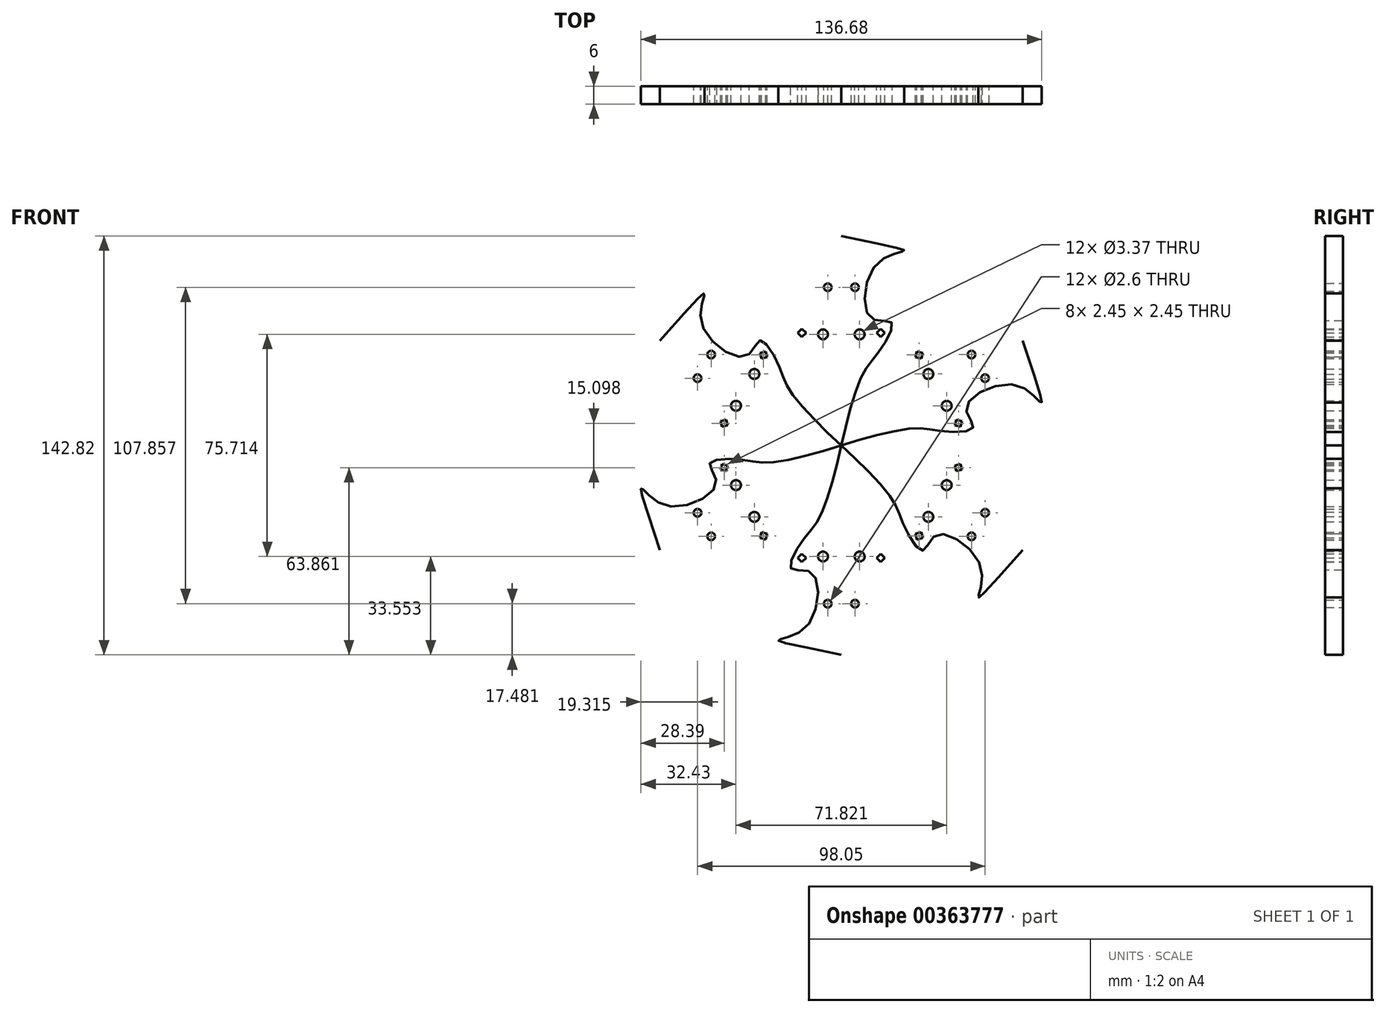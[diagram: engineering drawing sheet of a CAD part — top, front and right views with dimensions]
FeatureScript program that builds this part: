
annotation { "Feature Type Name" : "Feature", "Feature Type Description" : "" }
export const myFeature = defineFeature(function(context is Context, id is Id, definition is map)
    precondition{}
    {
        {
            var Q0;
            Q0=qCreatedBy(makeId("Front.planeOp"),FACE);
            var sketch = newSketch(context, id + "F0", { "sketchPlane" : qUnion([Q0])});
            skLineSegment(sketch, "E0", {"start": v(0, 0) * mm, "end": v(0, 66.43) * mm, "construction": true});
            skFitSpline(sketch, "E1", {"points": [v(0, 71.4) * mm, v(20.6, 65.97) * mm, v(11.17, 60.88) * mm, v(10.13, 43.35) * mm, v(17.12, 41.96) * mm, v(12.86, 32) * mm, v(7.45, 24.61) * mm, v(0, 0) * mm], "startDerivative": vector(349.85, -73.2) * mm, "endDerivative": vector(-30.6, -141.84) * mm});
            skCircle(sketch, "E2", {"center": v(6.25, 37.86) * mm, "radius": 1.68 * mm});
            skCircle(sketch, "E3", {"center": v(4.64, 53.93) * mm, "radius": 1.3 * mm});
            skLineSegment(sketch, "E4.bottom", {"start": v(-13.44, 39.79) * mm, "end": v(-12.02, 38.37) * mm});
            skLineSegment(sketch, "E4.top", {"start": v(-14.85, 38.37) * mm, "end": v(-13.44, 36.96) * mm});
            skLineSegment(sketch, "E4.left", {"start": v(-13.44, 39.79) * mm, "end": v(-14.85, 38.37) * mm});
            skLineSegment(sketch, "E4.right", {"start": v(-12.02, 38.37) * mm, "end": v(-13.44, 36.96) * mm});
            skLineSegment(sketch, "E5.MirrorCS", {"start": v(12.02, 38.37) * mm, "end": v(13.44, 36.96) * mm});
            skLineSegment(sketch, "E6.MirrorCS", {"start": v(13.44, 39.79) * mm, "end": v(14.85, 38.37) * mm});
            skLineSegment(sketch, "E7.MirrorCS", {"start": v(14.85, 38.37) * mm, "end": v(13.44, 36.96) * mm});
            skLineSegment(sketch, "E8.MirrorCS", {"start": v(13.44, 39.79) * mm, "end": v(12.02, 38.37) * mm});
            skCircle(sketch, "E9.MirrorC", {"center": v(-4.64, 53.93) * mm, "radius": 1.3 * mm});
            skCircle(sketch, "E10.MirrorC", {"center": v(-6.25, 37.86) * mm, "radius": 1.68 * mm});
            skFitSpline(sketch, "E11.MirrorCS", {"points": [v(0, 71.4) * mm, v(-20.6, 65.97) * mm, v(-11.17, 60.88) * mm, v(-10.13, 43.35) * mm, v(-17.12, 41.96) * mm, v(-12.86, 32) * mm, v(-7.45, 24.61) * mm, v(0, 0) * mm], "startDerivative": vector(-349.85, -73.2) * mm, "endDerivative": vector(30.6, -141.84) * mm});
            skSolve(sketch);
        }
        {
            var Q0;
            Q0 = qSketchRegion(id + "F0", true);
            extrude(context, id + "F1", {"entities" : qUnion([Q0]), "depth" : 6 * mm});
        }
        {
            var Q0;
            Q0=qCreatedBy(makeId("Right.planeOp"),FACE);
            var sketch = newSketch(context, id + "F2", { "sketchPlane" : qUnion([Q0])});
            skLineSegment(sketch, "E12", {"start": v(0, 0) * mm, "end": v(-63.75, 0) * mm, "construction": true});
            skSolve(sketch);
        }
        {
            var Q0;
            Q0=makeQuery(id+"F1.opExtrude","SWEPT_BODY",BODY,{"disambiguationData":[OSD([sQuery(id+"F0.wireOp",EDGE,"E1"),sQuery(id+"F0.wireOp",EDGE,"E2"),sQuery(id+"F0.wireOp",EDGE,"E3"),sQuery(id+"F0.wireOp",EDGE,"E4.bottom"),sQuery(id+"F0.wireOp",EDGE,"E4.top"),sQuery(id+"F0.wireOp",EDGE,"E4.left"),sQuery(id+"F0.wireOp",EDGE,"E4.right"),sQuery(id+"F0.wireOp",EDGE,"E5.MirrorCS"),sQuery(id+"F0.wireOp",EDGE,"E6.MirrorCS"),sQuery(id+"F0.wireOp",EDGE,"E7.MirrorCS"),sQuery(id+"F0.wireOp",EDGE,"E8.MirrorCS"),sQuery(id+"F0.wireOp",EDGE,"E9.MirrorC"),sQuery(id+"F0.wireOp",EDGE,"E10.MirrorC"),sQuery(id+"F0.wireOp",EDGE,"E11.MirrorCS")])]});
            var Q1;
            Q1=sQuery(id+"F2.wireOp",EDGE,"E12");
            circularPattern(context, id + "F3", {"entities" : qUnion([Q0]), "axis" : qUnion([Q1]), "angle" : 360 * degree, "instanceCount" : 6, "equalSpace" : true});
        }
    });
